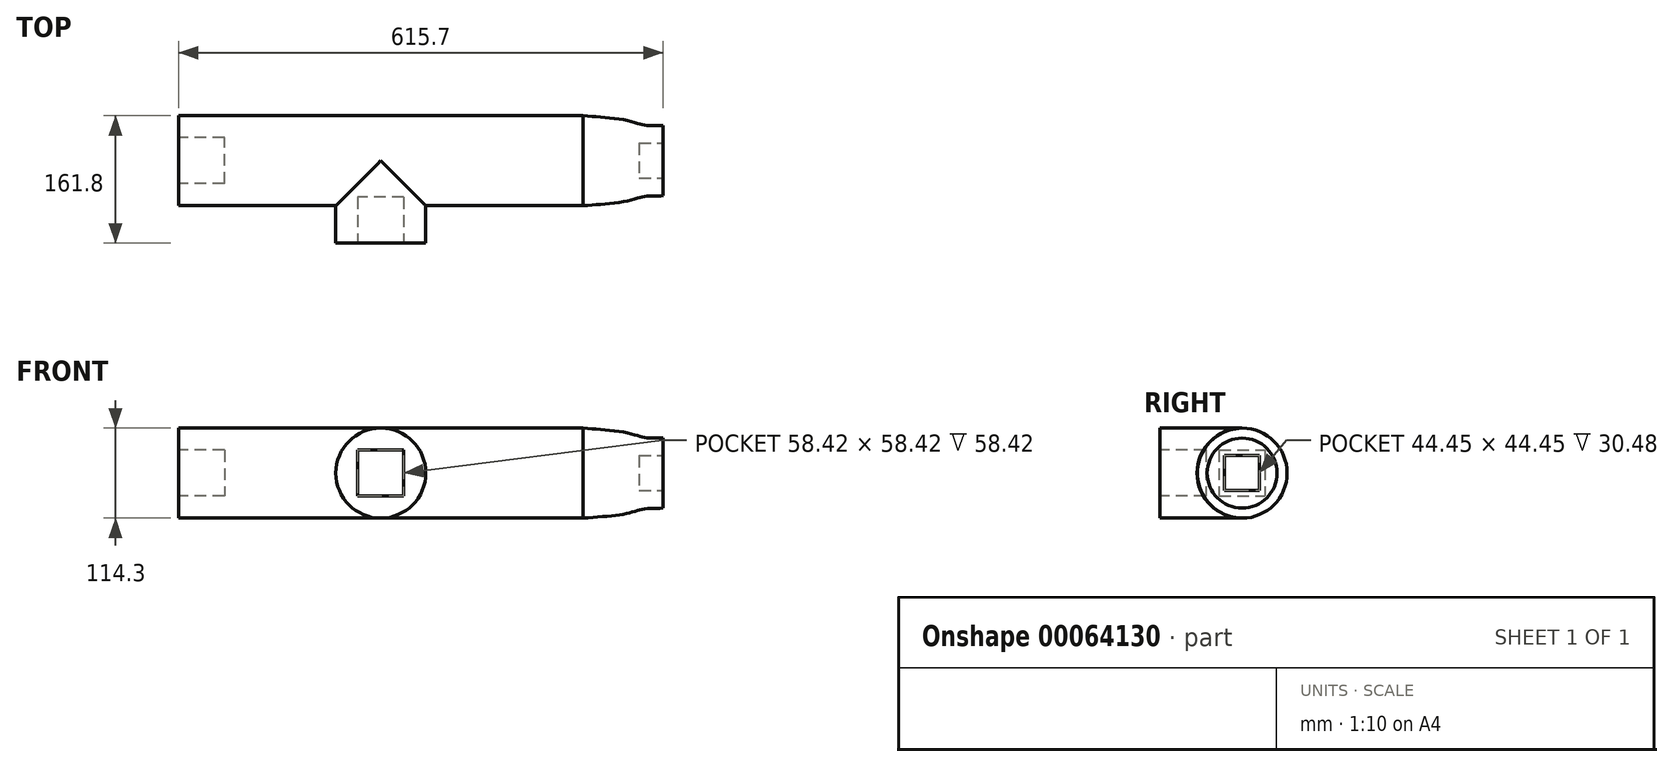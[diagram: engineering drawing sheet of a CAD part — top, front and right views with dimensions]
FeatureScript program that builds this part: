
annotation { "Feature Type Name" : "Feature", "Feature Type Description" : "" }
export const myFeature = defineFeature(function(context is Context, id is Id, definition is map)
    precondition{}
    {
        {
            var Q0;
            Q0=qCreatedBy(makeId("Right.planeOp"),FACE);
            var sketch = newSketch(context, id + "F0", { "sketchPlane" : qUnion([Q0])});
            skCircle(sketch, "E0", {"center": v(0, 0) * mm, "radius": 57.15 * mm});
            skSolve(sketch);
        }
        {
            var Q0;
            Q0=qCreatedBy(makeId("Top.planeOp"),FACE);
            var sketch = newSketch(context, id + "F1", { "sketchPlane" : qUnion([Q0])});
            skLineSegment(sketch, "E1", {"start": v(0, 0) * mm, "end": v(514.1, 0) * mm, "construction": true});
            skLineSegment(sketch, "E2", {"start": v(514.1, 0) * mm, "end": v(514.1, 57.15) * mm});
            skLineSegment(sketch, "E3", {"start": v(615.7, 0) * mm, "end": v(615.7, 44.45) * mm});
            skLineSegment(sketch, "E4", {"start": v(615.7, 0) * mm, "end": v(514.1, 0) * mm});
            skFitSpline(sketch, "E5", {"points": [v(514.1, 57.15) * mm, v(559.34, 53.08) * mm, v(580.7, 48.34) * mm, v(594.24, 45.06) * mm, v(615.7, 44.45) * mm], "startDerivative": vector(142.73, -11.85) * mm, "endDerivative": vector(94.53, -4.79) * mm});
            skSolve(sketch);
        }
        {
            var Q0;
            Q0=qCreatedBy(makeId("Front.planeOp"),FACE);
            var sketch = newSketch(context, id + "F2", { "sketchPlane" : qUnion([Q0])});
            skLineSegment(sketch, "E6", {"start": v(0, 0) * mm, "end": v(257.05, 0) * mm, "construction": true});
            skCircle(sketch, "E7", {"center": v(257.05, 0) * mm, "radius": 57.15 * mm});
            skSolve(sketch);
        }
        {
            var Q0;
            Q0 = qSketchRegion(id + "FnIMq1Pq2dPj32w_0", true);
            var Q1;
            Q1=makeQuery(id+"F0.imprint","IMPRINT",FACE,{"disambiguationData":[TD([[makeQuery(id+"F0.imprint","IMPRINT",EDGE,{"derivedFrom":sQuery(id+"F0.wireOp",EDGE,"E0")}),1.0]])]});
            extrude(context, id + "F3", {"entities" : qUnion([Q0, Q1]), "depth" : 514.1 * mm});
        }
        {
            var Q0;
            Q0=makeQuery(id+"F1.imprint","IMPRINT",FACE,{"disambiguationData":[TD([[makeQuery(id+"F1.imprint","IMPRINT",EDGE,{"derivedFrom":sQuery(id+"F1.wireOp",EDGE,"E2")}),-1.0]])]});
            var Q1;
            Q1=sQuery(id+"F1.wireOp",EDGE,"E4");
            revolve(context, id + "F4", {"operationType" : NewBodyOperationType.ADD, "entities" : qUnion([Q0]), "axis" : qUnion([Q1]), "revolveType" : RevolveType.FULL});
        }
        {
            var Q0;
            Q0 = qSketchRegion(id + "F2", true);
            extrude(context, id + "F5", {"entities" : qUnion([Q0]), "operationType" : NewBodyOperationType.ADD, "depth" : 104.65 * mm});
        }
        {
            var Q0;
            Q0=makeQuery(id+"F3.opExtrude","CAP_FACE",FACE,{"disambiguationData":[OSD([sQuery(id+"F0.wireOp",EDGE,"E0")])],"isStart":true});
            var sketch = newSketch(context, id + "F6", { "sketchPlane" : qUnion([Q0])});
            skLineSegment(sketch, "E8.bottom", {"start": v(29.21, 29.2) * mm, "end": v(-29.21, 29.2) * mm});
            skLineSegment(sketch, "E8.top", {"start": v(29.21, -29.21) * mm, "end": v(-29.21, -29.21) * mm});
            skLineSegment(sketch, "E8.left", {"start": v(29.21, 29.21) * mm, "end": v(29.21, -29.21) * mm});
            skLineSegment(sketch, "E8.right", {"start": v(-29.2, 29.21) * mm, "end": v(-29.21, -29.21) * mm});
            skPoint(sketch, "E8.middle", {"position": v(0, 0) * mm});
            skSolve(sketch);
        }
        {
            var Q0;
            Q0=makeQuery(id+"F6.imprint","IMPRINT",FACE,{"disambiguationData":[TD([[makeQuery(id+"F6.imprint","IMPRINT",EDGE,{"derivedFrom":sQuery(id+"F6.wireOp",EDGE,"E8.bottom")}),1.0]])]});
            extrude(context, id + "F7", {"entities" : qUnion([Q0]), "operationType" : NewBodyOperationType.REMOVE, "oppositeDirection" : true, "depth" : 58.42 * mm});
        }
        {
            var Q0;
            Q0=makeQuery(id+"F5.opExtrude","CAP_FACE",FACE,{"disambiguationData":[OSD([sQuery(id+"F2.wireOp",EDGE,"E7")])],"isStart":false});
            var sketch = newSketch(context, id + "F8", { "sketchPlane" : qUnion([Q0])});
            skLineSegment(sketch, "E9.bottom", {"start": v(286.26, 29.2) * mm, "end": v(227.84, 29.2) * mm});
            skLineSegment(sketch, "E9.top", {"start": v(286.26, -29.21) * mm, "end": v(227.84, -29.21) * mm});
            skLineSegment(sketch, "E9.left", {"start": v(286.26, 29.2) * mm, "end": v(286.26, -29.21) * mm});
            skLineSegment(sketch, "E9.right", {"start": v(227.84, 29.2) * mm, "end": v(227.84, -29.21) * mm});
            skPoint(sketch, "E9.middle", {"position": v(257.05, 0) * mm});
            skSolve(sketch);
        }
        {
            var Q0;
            Q0=makeQuery(id+"F8.imprint","IMPRINT",FACE,{"disambiguationData":[TD([[makeQuery(id+"F8.imprint","IMPRINT",EDGE,{"derivedFrom":sQuery(id+"F8.wireOp",EDGE,"E9.bottom")}),1.0]])]});
            extrude(context, id + "F9", {"entities" : qUnion([Q0]), "operationType" : NewBodyOperationType.REMOVE, "oppositeDirection" : true, "depth" : 58.42 * mm});
        }
        {
            var Q0;
            Q0=makeQuery(id+"F4.opRevolve","SWEPT_FACE",FACE,{"disambiguationData":[OSD([sQuery(id+"F1.wireOp",EDGE,"E3")])]});
            var sketch = newSketch(context, id + "F10", { "sketchPlane" : qUnion([Q0])});
            skLineSegment(sketch, "E10.bottom", {"start": v(22.22, 22.23) * mm, "end": v(-22.23, 22.23) * mm});
            skLineSegment(sketch, "E10.top", {"start": v(22.23, -22.23) * mm, "end": v(-22.22, -22.23) * mm});
            skLineSegment(sketch, "E10.left", {"start": v(22.22, 22.23) * mm, "end": v(22.23, -22.23) * mm});
            skLineSegment(sketch, "E10.right", {"start": v(-22.23, 22.23) * mm, "end": v(-22.22, -22.23) * mm});
            skPoint(sketch, "E10.middle", {"position": v(0, 0) * mm});
            skSolve(sketch);
        }
        {
            var Q0;
            Q0=makeQuery(id+"F10.imprint","IMPRINT",FACE,{"disambiguationData":[TD([[makeQuery(id+"F10.imprint","IMPRINT",EDGE,{"derivedFrom":sQuery(id+"F10.wireOp",EDGE,"E10.bottom")}),1.0]])]});
            extrude(context, id + "F11", {"entities" : qUnion([Q0]), "operationType" : NewBodyOperationType.REMOVE, "oppositeDirection" : true, "depth" : 30.48 * mm, "offsetDistance" : 25.4 * mm});
        }
    });
